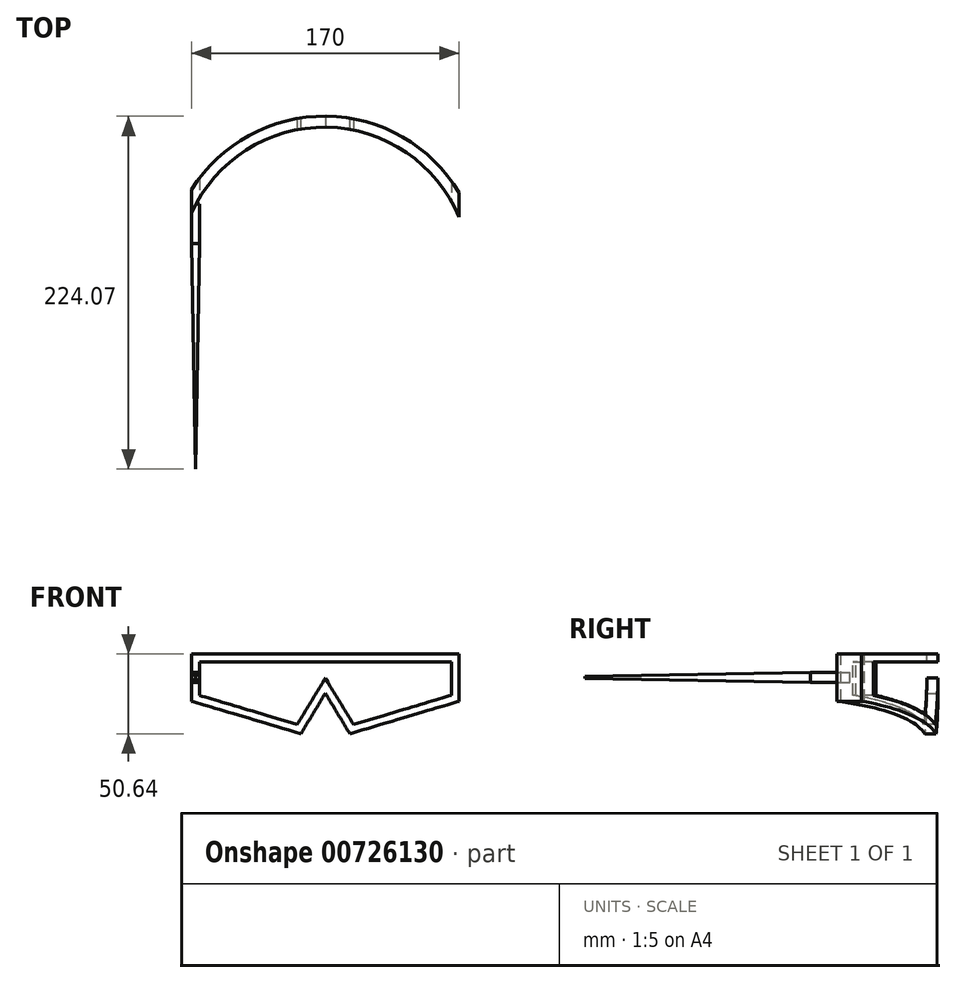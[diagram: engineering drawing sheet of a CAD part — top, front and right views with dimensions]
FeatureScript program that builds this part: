
annotation { "Feature Type Name" : "Feature", "Feature Type Description" : "" }
export const myFeature = defineFeature(function(context is Context, id is Id, definition is map)
    precondition{}
    {
        {
            var Q0;
            Q0=qCreatedBy(makeId("Front.planeOp"),FACE);
            var sketch = newSketch(context, id + "F0", { "sketchPlane" : qUnion([Q0])});
            skLineSegment(sketch, "E0.top", {"start": v(0.3, 25.88) * mm, "end": v(-84.7, 25.88) * mm});
            skLineSegment(sketch, "E0.right", {"start": v(-84.7, -4.12) * mm, "end": v(-84.7, 25.88) * mm});
            skPoint(sketch, "E0.middle", {"position": v(-42.2, -4.6) * mm});
            skLineSegment(sketch, "E1", {"start": v(-15.27, -24.76) * mm, "end": v(0.3, 0.88) * mm});
            skLineSegment(sketch, "E2", {"start": v(-15.27, -24.76) * mm, "end": v(-84.7, -4.12) * mm});
            skPoint(sketch, "E3.orphan", {"position": v(-84.7, -35.08) * mm});
            skPoint(sketch, "E4.orphan", {"position": v(0.3, -35.08) * mm});
            skPoint(sketch, "E5.middle", {"position": v(0.94, 33.45) * mm});
            skPoint(sketch, "E6.orphan", {"position": v(-41.56, 5.6) * mm});
            skPoint(sketch, "E7.orphan", {"position": v(43.44, 5.6) * mm});
            skLineSegment(sketch, "E8.MirrorCS", {"start": v(15.87, -24.76) * mm, "end": v(0.3, 0.88) * mm});
            skLineSegment(sketch, "E9.MirrorCS", {"start": v(15.87, -24.76) * mm, "end": v(85.3, -4.12) * mm});
            skLineSegment(sketch, "E10.MirrorCS", {"start": v(85.3, -4.12) * mm, "end": v(85.3, 25.88) * mm});
            skLineSegment(sketch, "E11.MirrorCS", {"start": v(0.3, 25.88) * mm, "end": v(85.3, 25.88) * mm});
            skPoint(sketch, "E12.orphan", {"position": v(-87.16, -3.39) * mm});
            skPoint(sketch, "E13.orphan", {"position": v(87.76, -3.39) * mm});
            skSolve(sketch);
        }
        {
            var Q0;
            Q0 = qSketchRegion(id + "F0", true);
            extrude(context, id + "F1", {"entities" : qUnion([Q0]), "endBound" : BoundingType.SYMMETRIC, "depth" : 150 * mm, "offsetDistance" : 25 * mm});
        }
        {
            var Q0;
            Q0=makeQuery(id+"F1.opExtrude","CAP_FACE",FACE,{"disambiguationData":[OSD([sQuery(id+"F0.wireOp",EDGE,"E0.top"),sQuery(id+"F0.wireOp",EDGE,"E0.right"),sQuery(id+"F0.wireOp",EDGE,"E1"),sQuery(id+"F0.wireOp",EDGE,"E2"),sQuery(id+"F0.wireOp",EDGE,"E8.MirrorCS"),sQuery(id+"F0.wireOp",EDGE,"E9.MirrorCS"),sQuery(id+"F0.wireOp",EDGE,"E10.MirrorCS"),sQuery(id+"F0.wireOp",EDGE,"E11.MirrorCS")])],"isStart":false});
            var sketch = newSketch(context, id + "F2", { "sketchPlane" : qUnion([Q0])});
            skLineSegment(sketch, "E14.0", {"start": v(0.3, 10.52) * mm, "end": v(18.14, -18.87) * mm});
            skLineSegment(sketch, "E14.1", {"start": v(-17.54, -18.87) * mm, "end": v(0.3, 10.52) * mm});
            skLineSegment(sketch, "E14.2", {"start": v(80.3, -0.39) * mm, "end": v(80.3, 20.88) * mm});
            skLineSegment(sketch, "E14.3", {"start": v(80.3, 20.88) * mm, "end": v(-79.7, 20.88) * mm});
            skLineSegment(sketch, "E14.4", {"start": v(-79.7, 20.88) * mm, "end": v(-79.7, -0.39) * mm});
            skLineSegment(sketch, "E14.5", {"start": v(18.14, -18.87) * mm, "end": v(80.3, -0.39) * mm});
            skLineSegment(sketch, "E14.6", {"start": v(-79.7, -0.39) * mm, "end": v(-17.54, -18.87) * mm});
            skSolve(sketch);
        }
        {
            var Q0;
            Q0 = qSketchRegion(id + "F2", true);
            extrude(context, id + "F3", {"entities" : qUnion([Q0]), "operationType" : NewBodyOperationType.REMOVE, "oppositeDirection" : true, "depth" : 200 * mm, "offsetDistance" : 25 * mm});
        }
        {
            var Q0;
            Q0=makeQuery(id+"F1.opExtrude","SWEPT_FACE",FACE,{"disambiguationData":[OSD([sQuery(id+"F0.wireOp",EDGE,"E0.top"),sQuery(id+"F0.wireOp",EDGE,"E11.MirrorCS")])]});
            var sketch = newSketch(context, id + "F4", { "sketchPlane" : qUnion([Q0])});
            skArc(sketch, "E15", {"start": v(99.3, -26.96) * mm, "mid": v(-3.95, 68.28) * mm, "end": v(-99.88, -34.33) * mm});
            skArc(sketch, "E16.0", {"start": v(92.3, -27.27) * mm, "mid": v(-3.7, 61.29) * mm, "end": v(-92.88, -34.12) * mm});
            skLineSegment(sketch, "E17", {"start": v(-99.88, -34.33) * mm, "end": v(-92.88, -34.12) * mm});
            skLineSegment(sketch, "E18", {"start": v(92.3, -27.27) * mm, "end": v(99.3, -26.96) * mm});
            skSolve(sketch);
        }
        {
            var Q0;
            Q0 = qSketchRegion(id + "F4", true);
            extrude(context, id + "F5", {"entities" : qUnion([Q0]), "operationType" : NewBodyOperationType.INTERSECT, "oppositeDirection" : true, "depth" : 100 * mm, "offsetDistance" : 25 * mm});
        }
        {
            var Q0;
            Q0=qCreatedBy(makeId("Front.planeOp"),FACE);
            var sketch = newSketch(context, id + "F6", { "sketchPlane" : qUnion([Q0])});
            skLineSegment(sketch, "E19.bottom", {"start": v(-79.69, 7.91) * mm, "end": v(-84.69, 7.91) * mm});
            skLineSegment(sketch, "E19.top", {"start": v(-79.69, 14.16) * mm, "end": v(-84.69, 14.16) * mm});
            skLineSegment(sketch, "E19.left", {"start": v(-79.69, 7.91) * mm, "end": v(-79.69, 14.16) * mm});
            skLineSegment(sketch, "E19.right", {"start": v(-84.69, 7.91) * mm, "end": v(-84.69, 14.16) * mm});
            skPoint(sketch, "E19.middle", {"position": v(-82.19, 11.04) * mm});
            skSolve(sketch);
        }
        {
            var Q0;
            Q0 = qSketchRegion(id + "F6", true);
            extrude(context, id + "F7", {"entities" : qUnion([Q0]), "operationType" : NewBodyOperationType.ADD, "endBound" : BoundingType.SYMMETRIC, "depth" : 25 * mm, "offsetDistance" : 25 * mm});
        }
        {
            var Q0;
            Q0=makeQuery(id+"F7.opExtrude","CAP_FACE",FACE,{"disambiguationData":[OSD([sQuery(id+"F6.wireOp",EDGE,"E19.bottom"),sQuery(id+"F6.wireOp",EDGE,"E19.top"),sQuery(id+"F6.wireOp",EDGE,"E19.left"),sQuery(id+"F6.wireOp",EDGE,"E19.right")])],"isStart":false});
            extrude(context, id + "F8", {"entities" : qUnion([Q0]), "operationType" : NewBodyOperationType.ADD, "depth" : 191.9 * mm, "offsetDistance" : 25 * mm, "hasDraft" : true, "draftAngle" : 1 * degree, "draftPullDirection" : true});
        }
    });
